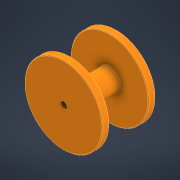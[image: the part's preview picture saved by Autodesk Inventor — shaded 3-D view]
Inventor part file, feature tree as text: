
AUTODESK INVENTOR PART (.ipt)
format: ipt  version: 2021 (Build 250183000, 183)  size: 158,208 bytes
history: native  units: mm
features: fillet x2, revolve x1, sketch x1
ambient origin geometry x8: Origin, YZ Plane, XZ Plane, XY Plane, X Axis, Y Axis, Z Axis, Center Point
bodies: Solid1 (feature_tree)
feature tree (4):
  revolve  "Revolution1"  [1 undecoded]
  fillet  "Fillet1"  Radius=55.0mm
  fillet  "Fillet2"  Radius=110.0mm
  sketch  "Sketch1"  dims[d6=20.0mm d7=20.0mm d10=55.0mm d11=110.0mm d14=90.0deg d15=10.0mm d16=30.0mm d17=110.0mm d18=110.0mm d19=2.0mm d20=2.0mm]
note: 1 required parameter value undecoded (feature->parameter linkage not recoverable at this tier; creation-order binding heuristic only, values carry confidence <= 0.55)
